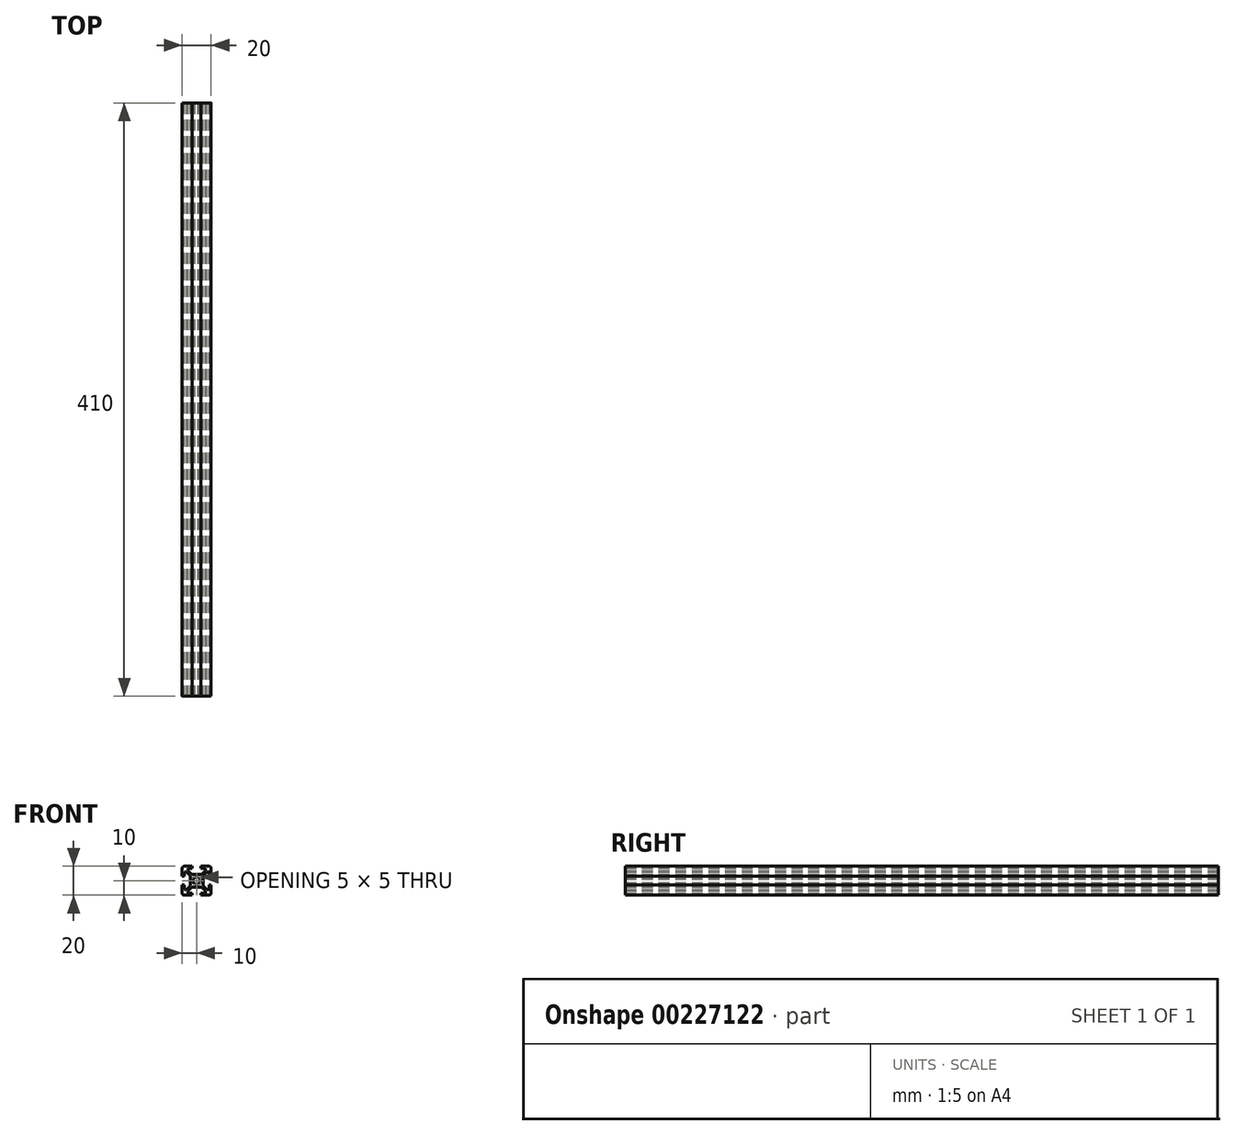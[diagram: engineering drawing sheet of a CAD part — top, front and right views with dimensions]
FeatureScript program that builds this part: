
annotation { "Feature Type Name" : "Feature", "Feature Type Description" : "" }
export const myFeature = defineFeature(function(context is Context, id is Id, definition is map)
    precondition{}
    {
        {
            var Q0;
            Q0=qCreatedBy(makeId("Front.planeOp"),FACE);
            var sketch = newSketch(context, id + "F0", { "sketchPlane" : qUnion([Q0])});
            skLineSegment(sketch, "E0.bottom", {"start": v(8.5, -10) * mm, "end": v(3, -10) * mm});
            skLineSegment(sketch, "E0.top", {"start": v(8.5, 10) * mm, "end": v(3, 10) * mm});
            skLineSegment(sketch, "E0.left", {"start": v(10, -8.5) * mm, "end": v(10, -3) * mm});
            skLineSegment(sketch, "E0.right", {"start": v(-10, -8.5) * mm, "end": v(-10, -3) * mm});
            skPoint(sketch, "E0.middle", {"position": v(0, 0) * mm});
            skLineSegment(sketch, "E1.bottom", {"start": v(6, -8.5) * mm, "end": v(3, -8.5) * mm});
            skLineSegment(sketch, "E1.top", {"start": v(6, 8.5) * mm, "end": v(3, 8.5) * mm});
            skLineSegment(sketch, "E1.left", {"start": v(8.5, -6) * mm, "end": v(8.5, -3) * mm});
            skLineSegment(sketch, "E1.right", {"start": v(-8.5, -6) * mm, "end": v(-8.5, -3) * mm});
            skLineSegment(sketch, "E2.bottom", {"start": v(3.44, -4.5) * mm, "end": v(-3.44, -4.5) * mm});
            skLineSegment(sketch, "E2.top", {"start": v(3.44, 4.5) * mm, "end": v(-3.44, 4.5) * mm});
            skLineSegment(sketch, "E2.left", {"start": v(4.5, -3.44) * mm, "end": v(4.5, 3.44) * mm});
            skLineSegment(sketch, "E2.right", {"start": v(-4.5, -3.44) * mm, "end": v(-4.5, 3.44) * mm});
            skLineSegment(sketch, "E3.bottom", {"start": v(8.5, -6) * mm, "end": v(7.06, -6) * mm});
            skLineSegment(sketch, "E3.top", {"start": v(8.5, 6) * mm, "end": v(7.06, 6) * mm});
            skLineSegment(sketch, "E4.left", {"start": v(6, -8.5) * mm, "end": v(6, -7.06) * mm});
            skLineSegment(sketch, "E4.right", {"start": v(-6, -8.5) * mm, "end": v(-6, -7.06) * mm});
            skPoint(sketch, "E5.orphan", {"position": v(-8.5, 8.5) * mm});
            skPoint(sketch, "E6.orphan", {"position": v(8.5, 8.5) * mm});
            skPoint(sketch, "E7.orphan", {"position": v(8.5, -8.5) * mm});
            skPoint(sketch, "E8.orphan", {"position": v(-8.5, -8.5) * mm});
            skLineSegment(sketch, "E9.trimOffspring", {"start": v(-6, 7.06) * mm, "end": v(-6, 8.5) * mm});
            skLineSegment(sketch, "E10.trimOffspring", {"start": v(-7.06, 6) * mm, "end": v(-8.5, 6) * mm});
            skLineSegment(sketch, "E11.trimOffspring", {"start": v(6, 7.06) * mm, "end": v(6, 8.5) * mm});
            skLineSegment(sketch, "E12.trimOffspring", {"start": v(-7.06, -6) * mm, "end": v(-8.5, -6) * mm});
            skLineSegment(sketch, "E13", {"start": v(-10, 10) * mm, "end": v(0, 0) * mm, "construction": true});
            skLineSegment(sketch, "E14", {"start": v(10, 10) * mm, "end": v(0, 0) * mm, "construction": true});
            skLineSegment(sketch, "E15", {"start": v(-6, 7.06) * mm, "end": v(-3.44, 4.5) * mm});
            skPoint(sketch, "E15.endSnap0", {"position": v(7.25, -6) * mm});
            skLineSegment(sketch, "E16", {"start": v(6, -7.06) * mm, "end": v(3.44, -4.5) * mm});
            skLineSegment(sketch, "E17", {"start": v(7.06, 6) * mm, "end": v(4.5, 3.44) * mm});
            skLineSegment(sketch, "E18", {"start": v(6, 7.06) * mm, "end": v(3.44, 4.5) * mm});
            skPoint(sketch, "E19.orphan", {"position": v(6, -6) * mm});
            skPoint(sketch, "E20.orphan", {"position": v(-4.5, -4.5) * mm});
            skPoint(sketch, "E21.orphan", {"position": v(-4.5, 4.5) * mm});
            skPoint(sketch, "E22.orphan", {"position": v(4.5, 4.5) * mm});
            skPoint(sketch, "E23.orphan", {"position": v(4.5, -4.5) * mm});
            skLineSegment(sketch, "E24.trimOffspring", {"start": v(4.5, -3.44) * mm, "end": v(7.06, -6) * mm});
            skLineSegment(sketch, "E25.trimOffspring", {"start": v(-3.44, -4.5) * mm, "end": v(-6, -7.06) * mm});
            skLineSegment(sketch, "E26.trimOffspring", {"start": v(-4.5, -3.44) * mm, "end": v(-7.06, -6) * mm});
            skLineSegment(sketch, "E27.trimOffspring", {"start": v(-4.5, 3.44) * mm, "end": v(-7.06, 6) * mm});
            skLineSegment(sketch, "E28.bottom", {"start": v(8.5, -3) * mm, "end": v(10, -3) * mm});
            skLineSegment(sketch, "E28.top", {"start": v(8.5, 3) * mm, "end": v(10, 3) * mm});
            skPoint(sketch, "E28.middle", {"position": v(10, 0) * mm});
            skLineSegment(sketch, "E29.left", {"start": v(3, 8.5) * mm, "end": v(3, 10) * mm});
            skLineSegment(sketch, "E29.right", {"start": v(-3, 8.5) * mm, "end": v(-3, 10) * mm});
            skPoint(sketch, "E29.middle", {"position": v(0, 10) * mm});
            skLineSegment(sketch, "E30.bottom", {"start": v(-8.5, 3) * mm, "end": v(-10, 3) * mm});
            skLineSegment(sketch, "E30.top", {"start": v(-8.5, -3) * mm, "end": v(-10, -3) * mm});
            skPoint(sketch, "E30.middle", {"position": v(-10, 0) * mm});
            skLineSegment(sketch, "E31.left", {"start": v(3, -8.5) * mm, "end": v(3, -10) * mm});
            skLineSegment(sketch, "E31.right", {"start": v(-3, -8.5) * mm, "end": v(-3, -10) * mm});
            skPoint(sketch, "E31.middle", {"position": v(0, -10) * mm});
            skPoint(sketch, "E32.orphan", {"position": v(3, 11.5) * mm});
            skPoint(sketch, "E33.orphan", {"position": v(-3, 11.5) * mm});
            skLineSegment(sketch, "E34.trimOffspring", {"start": v(-3, 10) * mm, "end": v(-8.5, 10) * mm});
            skLineSegment(sketch, "E35.trimOffspring", {"start": v(-3, 8.5) * mm, "end": v(-6, 8.5) * mm});
            skPoint(sketch, "E28.right.end.orphan", {"position": v(11.5, 3) * mm});
            skPoint(sketch, "E36.orphan", {"position": v(11.5, -3) * mm});
            skLineSegment(sketch, "E37.trimOffspring", {"start": v(10, 3) * mm, "end": v(10, 8.5) * mm});
            skLineSegment(sketch, "E38.trimOffspring", {"start": v(8.5, 3) * mm, "end": v(8.5, 6) * mm});
            skPoint(sketch, "E39.orphan", {"position": v(3, -11.5) * mm});
            skPoint(sketch, "E40.orphan", {"position": v(-3, -11.5) * mm});
            skLineSegment(sketch, "E41.trimOffspring", {"start": v(-3, -10) * mm, "end": v(-8.5, -10) * mm});
            skLineSegment(sketch, "E42.trimOffspring", {"start": v(-3, -8.5) * mm, "end": v(-6, -8.5) * mm});
            skPoint(sketch, "E30.right.end.orphan", {"position": v(-11.5, -3) * mm});
            skPoint(sketch, "E43.orphan", {"position": v(-11.5, 3) * mm});
            skLineSegment(sketch, "E44.trimOffspring", {"start": v(-10, 3) * mm, "end": v(-10, 8.5) * mm});
            skLineSegment(sketch, "E45.trimOffspring", {"start": v(-8.5, 3) * mm, "end": v(-8.5, 6) * mm});
            skLineSegment(sketch, "E46.trimOffspring", {"start": v(0, 0) * mm, "end": v(10, -10) * mm, "construction": true});
            skLineSegment(sketch, "E47.trimOffspring", {"start": v(0, 0) * mm, "end": v(-10, -10) * mm, "construction": true});
            skArc(sketch, "E48", {"start": v(1.16, 2.22) * mm, "mid": v(0, 2.5) * mm, "end": v(-1.16, 2.22) * mm});
            skLineSegment(sketch, "E49", {"start": v(-2.5, -1.44) * mm, "end": v(1.44, 2.5) * mm});
            skLineSegment(sketch, "E50", {"start": v(2.5, 1.44) * mm, "end": v(-1.44, -2.5) * mm});
            skLineSegment(sketch, "E51", {"start": v(1.44, -2.5) * mm, "end": v(-2.5, 1.44) * mm});
            skLineSegment(sketch, "E52", {"start": v(-1.44, 2.5) * mm, "end": v(2.5, -1.44) * mm});
            skLineSegment(sketch, "E53", {"start": v(2.5, 1.44) * mm, "end": v(2.5, -1.44) * mm, "construction": true});
            skLineSegment(sketch, "E54", {"start": v(1.44, -2.5) * mm, "end": v(-1.44, -2.5) * mm, "construction": true});
            skLineSegment(sketch, "E55", {"start": v(-2.5, -1.44) * mm, "end": v(-2.5, 1.44) * mm, "construction": true});
            skLineSegment(sketch, "E56", {"start": v(-1.44, 2.5) * mm, "end": v(1.44, 2.5) * mm, "construction": true});
            skLineSegment(sketch, "E57", {"start": v(-1.44, 2.5) * mm, "end": v(-2.5, 1.44) * mm});
            skLineSegment(sketch, "E58", {"start": v(1.44, 2.5) * mm, "end": v(2.5, 1.44) * mm});
            skLineSegment(sketch, "E59", {"start": v(2.5, -1.44) * mm, "end": v(1.44, -2.5) * mm});
            skLineSegment(sketch, "E60", {"start": v(-1.44, -2.5) * mm, "end": v(-2.5, -1.44) * mm});
            skArc(sketch, "E61.trimOffspring", {"start": v(-2.22, 1.16) * mm, "mid": v(-2.5, 0) * mm, "end": v(-2.22, -1.16) * mm});
            skArc(sketch, "E62.trimOffspring", {"start": v(-1.16, -2.22) * mm, "mid": v(0, -2.5) * mm, "end": v(1.16, -2.22) * mm});
            skArc(sketch, "E63.trimOffspring", {"start": v(2.22, -1.16) * mm, "mid": v(2.5, 0) * mm, "end": v(2.22, 1.16) * mm});
            skPoint(sketch, "E64.visualSharp", {"position": v(10, 10) * mm});
            skArc(sketch, "E64.filletArc", {"start": v(10, 8.5) * mm, "mid": v(9.56, 9.56) * mm, "end": v(8.5, 10) * mm});
            skPoint(sketch, "E65.visualSharp", {"position": v(10, -10) * mm});
            skArc(sketch, "E65.filletArc", {"start": v(8.5, -10) * mm, "mid": v(9.56, -9.56) * mm, "end": v(10, -8.5) * mm});
            skPoint(sketch, "E66.visualSharp", {"position": v(-10, -10) * mm});
            skArc(sketch, "E66.filletArc", {"start": v(-10, -8.5) * mm, "mid": v(-9.56, -9.56) * mm, "end": v(-8.5, -10) * mm});
            skPoint(sketch, "E67.visualSharp", {"position": v(-10, 10) * mm});
            skArc(sketch, "E67.filletArc", {"start": v(-8.5, 10) * mm, "mid": v(-9.56, 9.56) * mm, "end": v(-10, 8.5) * mm});
            skSolve(sketch);
        }
        {
            assignVariable(context, id + "F2", {"name" : "Length", "anyValue" : 410});
        }
        {
            var Q0;
            Q0=qSketchRegion(id+"F0",true);
            extrude(context, id + "F1", {"entities" : qUnion([Q0]), "depth" : (getVariable(context, 'Length')) * mm});
        }
    });
